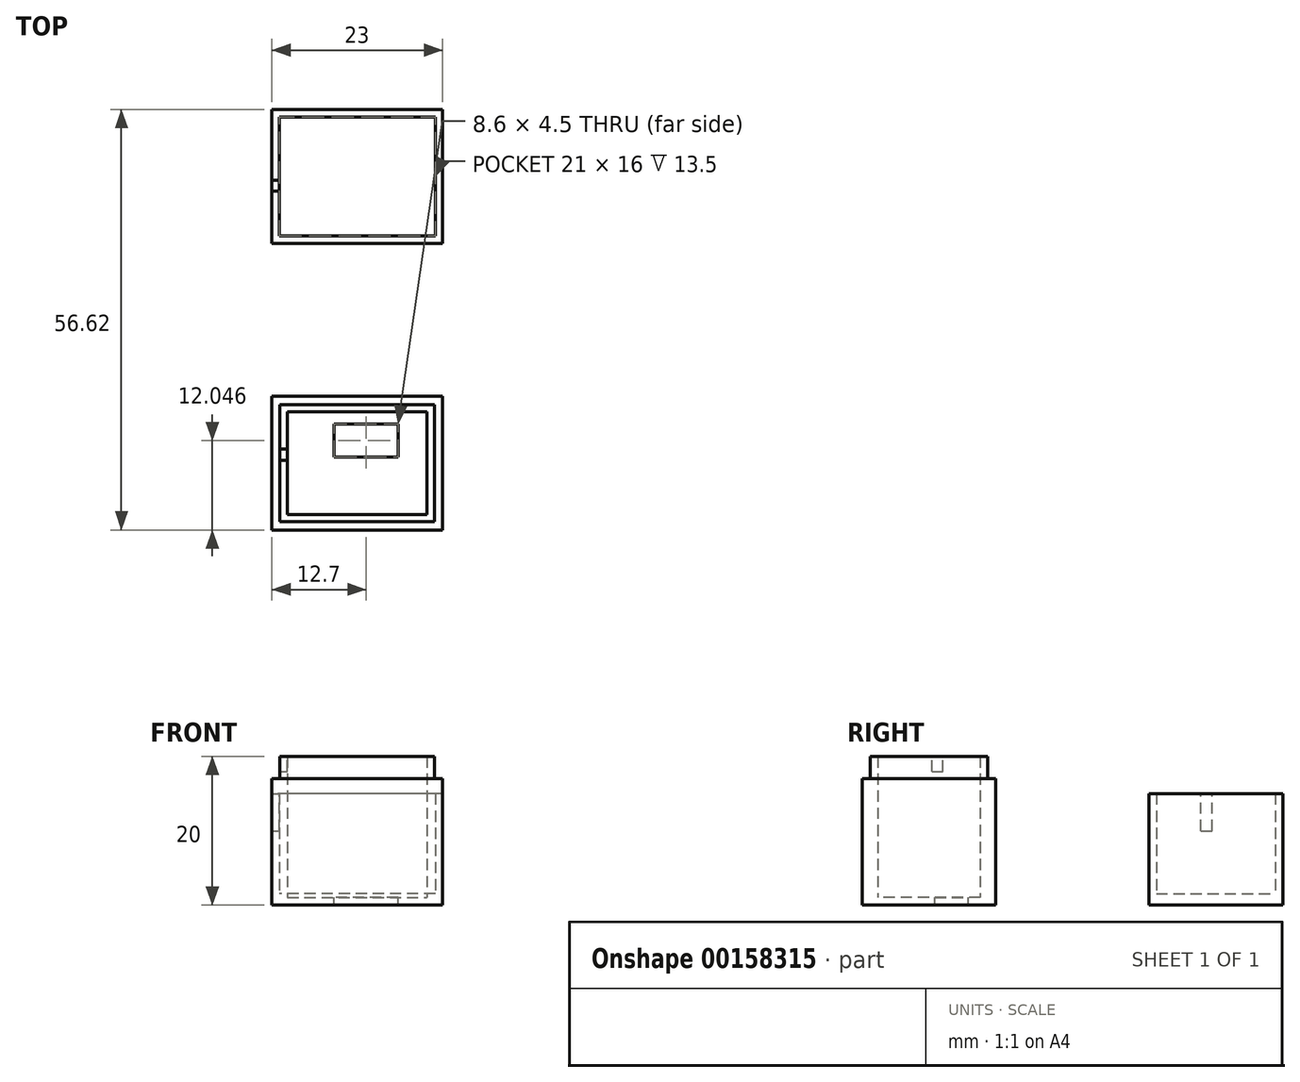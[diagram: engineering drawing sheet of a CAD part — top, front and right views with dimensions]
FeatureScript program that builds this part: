
annotation { "Feature Type Name" : "Feature", "Feature Type Description" : "" }
export const myFeature = defineFeature(function(context is Context, id is Id, definition is map)
    precondition{}
    {
        {
            var Q0;
            Q0=qCreatedBy(makeId("Top.planeOp"),FACE);
            var sketch = newSketch(context, id + "F0", { "sketchPlane" : qUnion([Q0])});
            skLineSegment(sketch, "E0.bottom", {"start": v(10.5, -8) * mm, "end": v(-10.5, -8) * mm});
            skLineSegment(sketch, "E0.top", {"start": v(10.5, 8) * mm, "end": v(-10.5, 8) * mm});
            skLineSegment(sketch, "E0.left", {"start": v(10.5, -8) * mm, "end": v(10.5, 8) * mm});
            skLineSegment(sketch, "E0.right", {"start": v(-10.5, -8) * mm, "end": v(-10.5, 8) * mm});
            skPoint(sketch, "E0.middle", {"position": v(0, 0) * mm});
            skLineSegment(sketch, "E1.0", {"start": v(11.5, 9) * mm, "end": v(-11.5, 9) * mm});
            skLineSegment(sketch, "E1.1", {"start": v(11.5, -9) * mm, "end": v(11.5, 9) * mm});
            skLineSegment(sketch, "E1.2", {"start": v(11.5, -9) * mm, "end": v(-11.5, -9) * mm});
            skLineSegment(sketch, "E1.3", {"start": v(-11.5, -9) * mm, "end": v(-11.5, 9) * mm});
            skSolve(sketch);
        }
        {
            var Q0;
            Q0=makeQuery(id+"F0.imprint","IMPRINT",FACE,{"disambiguationData":[TD([[makeQuery(id+"F0.imprint","IMPRINT",EDGE,{"derivedFrom":sQuery(id+"F0.wireOp",EDGE,"E0.bottom")}),-1.0]])]});
            extrude(context, id + "F1", {"entities" : qUnion([Q0]), "depth" : 1.5 * mm});
        }
        {
            var Q0;
            Q0=makeQuery(id+"F0.imprint","IMPRINT",FACE,{"disambiguationData":[TD([[makeQuery(id+"F0.imprint","IMPRINT",EDGE,{"derivedFrom":sQuery(id+"F0.wireOp",EDGE,"E0.bottom")}),1.0]])]});
            extrude(context, id + "F2", {"entities" : qUnion([Q0]), "operationType" : NewBodyOperationType.ADD, "depth" : 15 * mm});
        }
        {
            var Q0;
            Q0=makeQuery(id+"F2.opExtrude","CAP_FACE",FACE,{"disambiguationData":[OSD([sQuery(id+"F0.wireOp",EDGE,"E0.bottom"),sQuery(id+"F0.wireOp",EDGE,"E0.top"),sQuery(id+"F0.wireOp",EDGE,"E0.left"),sQuery(id+"F0.wireOp",EDGE,"E0.right"),sQuery(id+"F0.wireOp",EDGE,"E1.0"),sQuery(id+"F0.wireOp",EDGE,"E1.1"),sQuery(id+"F0.wireOp",EDGE,"E1.2"),sQuery(id+"F0.wireOp",EDGE,"E1.3")])],"isStart":false});
            var sketch = newSketch(context, id + "F3", { "sketchPlane" : qUnion([Q0])});
            skLineSegment(sketch, "E2.bottom", {"start": v(-11.5, -2) * mm, "end": v(-10.5, -2) * mm});
            skLineSegment(sketch, "E2.top", {"start": v(-11.5, -0.5) * mm, "end": v(-10.5, -0.5) * mm});
            skLineSegment(sketch, "E2.left", {"start": v(-11.5, -2) * mm, "end": v(-11.5, -0.5) * mm});
            skLineSegment(sketch, "E2.right", {"start": v(-10.5, -2) * mm, "end": v(-10.5, -0.5) * mm});
            skSolve(sketch);
        }
        {
            var Q0;
            Q0=makeQuery(id+"F3.imprint","IMPRINT",FACE,{"disambiguationData":[TD([[makeQuery(id+"F3.imprint","IMPRINT",EDGE,{"derivedFrom":sQuery(id+"F3.wireOp",EDGE,"E2.bottom")}),1.0]])]});
            extrude(context, id + "F4", {"entities" : qUnion([Q0]), "operationType" : NewBodyOperationType.REMOVE, "oppositeDirection" : true, "depth" : 5 * mm});
        }
        {
            var Q0;
            Q0=qCreatedBy(makeId("Top.planeOp"),FACE);
            var sketch = newSketch(context, id + "F5", { "sketchPlane" : qUnion([Q0])});
            skLineSegment(sketch, "E3.bottom", {"start": v(11.5, -47.62) * mm, "end": v(-11.5, -47.62) * mm});
            skLineSegment(sketch, "E3.top", {"start": v(11.5, -29.62) * mm, "end": v(-11.5, -29.62) * mm});
            skLineSegment(sketch, "E3.left", {"start": v(11.5, -47.62) * mm, "end": v(11.5, -29.62) * mm});
            skLineSegment(sketch, "E3.right", {"start": v(-11.5, -47.62) * mm, "end": v(-11.5, -29.62) * mm});
            skPoint(sketch, "E3.middle", {"position": v(0, -38.62) * mm});
            skLineSegment(sketch, "E4.0", {"start": v(-10.4, -46.52) * mm, "end": v(-10.4, -30.72) * mm});
            skLineSegment(sketch, "E4.1", {"start": v(10.4, -46.52) * mm, "end": v(-10.4, -46.52) * mm});
            skLineSegment(sketch, "E4.2", {"start": v(10.4, -46.52) * mm, "end": v(10.4, -30.72) * mm});
            skLineSegment(sketch, "E4.3", {"start": v(10.4, -30.72) * mm, "end": v(-10.4, -30.72) * mm});
            skLineSegment(sketch, "E5.0", {"start": v(9.4, -31.72) * mm, "end": v(-9.4, -31.72) * mm});
            skLineSegment(sketch, "E5.1", {"start": v(9.4, -45.52) * mm, "end": v(9.4, -31.72) * mm});
            skLineSegment(sketch, "E5.2", {"start": v(9.4, -45.52) * mm, "end": v(-9.4, -45.52) * mm});
            skLineSegment(sketch, "E5.3", {"start": v(-9.4, -45.52) * mm, "end": v(-9.4, -31.72) * mm});
            skLineSegment(sketch, "E6.left", {"start": v(-11.5, -45.92) * mm, "end": v(-11.5, -32.32) * mm});
            skLineSegment(sketch, "E6.right", {"start": v(-10.4, -45.92) * mm, "end": v(-10.4, -32.32) * mm});
            skSolve(sketch);
        }
        {
            var Q0;
            Q0=makeQuery(id+"F5.imprint","IMPRINT",FACE,{"disambiguationData":[TD([[makeQuery(id+"F5.imprint","IMPRINT",EDGE,{"derivedFrom":sQuery(id+"F5.wireOp",EDGE,"E3.bottom")}),-1.0]])]});
            var Q1;
            Q1=makeQuery(id+"F5.imprint","IMPRINT",FACE,{"disambiguationData":[TD([[makeQuery(id+"F5.imprint","IMPRINT",EDGE,{"derivedFrom":sQuery(id+"F5.wireOp",EDGE,"E4.0")}),-1.0]])]});
            var Q2;
            Q2=makeQuery(id+"F5.imprint","IMPRINT",FACE,{"disambiguationData":[TD([[makeQuery(id+"F5.imprint","IMPRINT",EDGE,{"derivedFrom":sQuery(id+"F5.wireOp",EDGE,"E5.0")}),1.0]])]});
            extrude(context, id + "F6", {"entities" : qUnion([Q0, Q1, Q2]), "depth" : 1 * mm});
        }
        {
            var Q0;
            Q0=makeQuery(id+"F5.imprint","IMPRINT",FACE,{"disambiguationData":[TD([[makeQuery(id+"F5.imprint","IMPRINT",EDGE,{"derivedFrom":sQuery(id+"F5.wireOp",EDGE,"E4.1")}),-1.0]])]});
            extrude(context, id + "F7", {"entities" : qUnion([Q0]), "operationType" : NewBodyOperationType.ADD, "depth" : 20 * mm});
        }
        {
            var Q0;
            Q0=makeQuery(id+"F7.boolean.opBoolean","SPLIT",FACE,{"disambiguationData":[TD([makeQuery(id+"F7.opExtrude","SWEPT_FACE",FACE,{"disambiguationData":[OSD([sQuery(id+"F5.wireOp",EDGE,"E5.0")])]})])],"derivedFrom":makeQuery(id+"F6.opExtrude","CAP_FACE",FACE,{"disambiguationData":[OSD([sQuery(id+"F5.wireOp",EDGE,"E3.bottom"),sQuery(id+"F5.wireOp",EDGE,"E3.top"),sQuery(id+"F5.wireOp",EDGE,"E3.left"),sQuery(id+"F5.wireOp",EDGE,"E3.right"),sQuery(id+"F5.wireOp",EDGE,"E6.left")])],"isStart":false})});
            var sketch = newSketch(context, id + "F8", { "sketchPlane" : qUnion([Q0])});
            skLineSegment(sketch, "E7.bottom", {"start": v(5.5, -37.82) * mm, "end": v(-3.1, -37.82) * mm});
            skLineSegment(sketch, "E7.top", {"start": v(5.5, -33.32) * mm, "end": v(-3.1, -33.32) * mm});
            skLineSegment(sketch, "E7.left", {"start": v(5.5, -37.82) * mm, "end": v(5.5, -33.32) * mm});
            skLineSegment(sketch, "E7.right", {"start": v(-3.1, -37.82) * mm, "end": v(-3.1, -33.32) * mm});
            skPoint(sketch, "E7.middle", {"position": v(1.2, -35.57) * mm});
            skSolve(sketch);
        }
        {
            var Q0;
            Q0=makeQuery(id+"F8.imprint","IMPRINT",FACE,{"disambiguationData":[TD([[makeQuery(id+"F8.imprint","IMPRINT",EDGE,{"derivedFrom":sQuery(id+"F8.wireOp",EDGE,"E7.bottom")}),-1.0]])]});
            extrude(context, id + "F9", {"entities" : qUnion([Q0]), "operationType" : NewBodyOperationType.REMOVE, "oppositeDirection" : true, "depth" : 4 * mm});
        }
        {
            var Q0;
            {var subQ0=sQuery(id+"F5.wireOp",EDGE,"E6.left");var subQ1=sQuery(id+"F5.wireOp",EDGE,"E3.right");var subQ2=sQuery(id+"F5.wireOp",EDGE,"E3.left");var subQ3=sQuery(id+"F5.wireOp",EDGE,"E3.top");var subQ4=sQuery(id+"F5.wireOp",EDGE,"E3.bottom");Q0=makeQuery(id+"F7.boolean.opBoolean","SPLIT",FACE,{"disambiguationData":[TD([makeQuery(id+"F6.opExtrude","SWEPT_FACE",FACE,{"disambiguationData":[OSD([subQ4])]})])],"derivedFrom":makeQuery(id+"F6.opExtrude","CAP_FACE",FACE,{"disambiguationData":[OSD([subQ4,subQ3,subQ2,subQ1,subQ0])],"isStart":false})});}
            extrude(context, id + "F10", {"entities" : qUnion([Q0]), "operationType" : NewBodyOperationType.ADD, "depth" : 16 * mm});
        }
        {
            var Q0;
            Q0=makeQuery(id+"F7.opExtrude","CAP_FACE",FACE,{"disambiguationData":[OSD([sQuery(id+"F5.wireOp",EDGE,"E4.0"),sQuery(id+"F5.wireOp",EDGE,"E4.1"),sQuery(id+"F5.wireOp",EDGE,"E4.2"),sQuery(id+"F5.wireOp",EDGE,"E4.3"),sQuery(id+"F5.wireOp",EDGE,"E5.0"),sQuery(id+"F5.wireOp",EDGE,"E5.1"),sQuery(id+"F5.wireOp",EDGE,"E5.2"),sQuery(id+"F5.wireOp",EDGE,"E5.3"),sQuery(id+"F5.wireOp",EDGE,"E6.right")])],"isStart":false});
            var sketch = newSketch(context, id + "F11", { "sketchPlane" : qUnion([Q0])});
            skLineSegment(sketch, "E8.bottom", {"start": v(-10.4, -38.22) * mm, "end": v(-9.4, -38.22) * mm});
            skLineSegment(sketch, "E8.top", {"start": v(-10.4, -36.72) * mm, "end": v(-9.4, -36.72) * mm});
            skLineSegment(sketch, "E8.left", {"start": v(-10.4, -38.22) * mm, "end": v(-10.4, -36.72) * mm});
            skLineSegment(sketch, "E8.right", {"start": v(-9.4, -38.22) * mm, "end": v(-9.4, -36.72) * mm});
            skSolve(sketch);
        }
        {
            var Q0;
            Q0=makeQuery(id+"F11.imprint","IMPRINT",FACE,{"disambiguationData":[TD([[makeQuery(id+"F11.imprint","IMPRINT",EDGE,{"derivedFrom":sQuery(id+"F11.wireOp",EDGE,"E8.bottom")}),1.0]])]});
            extrude(context, id + "F12", {"entities" : qUnion([Q0]), "operationType" : NewBodyOperationType.REMOVE, "oppositeDirection" : true, "depth" : 2 * mm});
        }
    });
